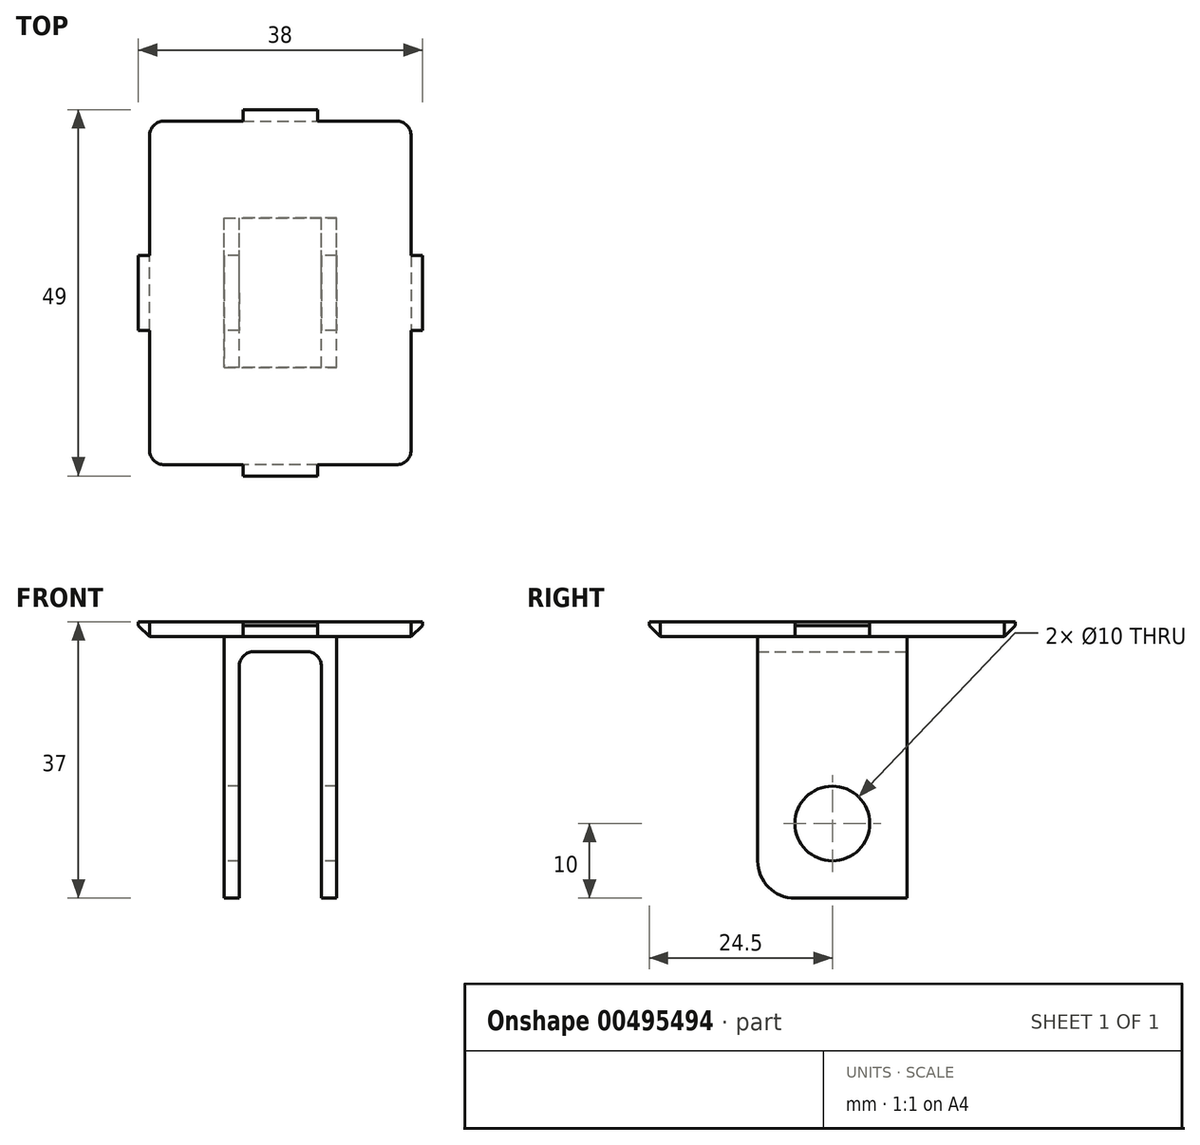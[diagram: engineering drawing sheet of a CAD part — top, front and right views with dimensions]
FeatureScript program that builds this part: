
annotation { "Feature Type Name" : "Feature", "Feature Type Description" : "" }
export const myFeature = defineFeature(function(context is Context, id is Id, definition is map)
    precondition{}
    {
        {
            var Q0;
            Q0=qCreatedBy(makeId("Front.planeOp"),FACE);
            var sketch = newSketch(context, id + "F0", { "sketchPlane" : qUnion([Q0])});
            skLineSegment(sketch, "E0", {"start": v(0, 71.67) * mm, "end": v(0, 0) * mm, "construction": true});
            skLineSegment(sketch, "E1", {"start": v(0, 0) * mm, "end": v(-98, 0) * mm, "construction": true});
            skLineSegment(sketch, "E2", {"start": v(0, 35) * mm, "end": v(-7.5, 35) * mm});
            skLineSegment(sketch, "E3", {"start": v(-7.5, 35) * mm, "end": v(-7.5, 0) * mm});
            skLineSegment(sketch, "E4", {"start": v(0, 33) * mm, "end": v(-3.5, 33) * mm});
            skLineSegment(sketch, "E5", {"start": v(-5.5, 31) * mm, "end": v(-5.5, 0) * mm});
            skLineSegment(sketch, "E6", {"start": v(-7.5, 0) * mm, "end": v(-5.5, 0) * mm});
            skPoint(sketch, "E7.visualSharp", {"position": v(-5.5, 33) * mm});
            skArc(sketch, "E7.filletArc", {"start": v(-3.5, 33) * mm, "mid": v(-4.91, 32.41) * mm, "end": v(-5.5, 31) * mm});
            skLineSegment(sketch, "E8.MirrorCS", {"start": v(0, 33) * mm, "end": v(3.5, 33) * mm});
            skLineSegment(sketch, "E9.MirrorCS", {"start": v(7.5, 0) * mm, "end": v(5.5, 0) * mm});
            skArc(sketch, "E10.MirrorCS", {"start": v(3.5, 33) * mm, "mid": v(4.91, 32.41) * mm, "end": v(5.5, 31) * mm});
            skLineSegment(sketch, "E11.MirrorCS", {"start": v(5.5, 31) * mm, "end": v(5.5, 0) * mm});
            skPoint(sketch, "E12.MirrorP", {"position": v(5.5, 33) * mm});
            skLineSegment(sketch, "E13.MirrorCS", {"start": v(0, 35) * mm, "end": v(7.5, 35) * mm});
            skLineSegment(sketch, "E14.MirrorCS", {"start": v(7.5, 35) * mm, "end": v(7.5, 0) * mm});
            skSolve(sketch);
        }
        {
            var Q0;
            Q0 = qSketchRegion(id + "F0", true);
            extrude(context, id + "F1", {"entities" : qUnion([Q0]), "depth" : 20 * mm});
        }
        {
            var Q0;
            Q0=makeQuery(id+"F1.opExtrude","SWEPT_FACE",FACE,{"disambiguationData":[OSD([sQuery(id+"F0.wireOp",EDGE,"E3")])]});
            var sketch = newSketch(context, id + "F2", { "sketchPlane" : qUnion([Q0])});
            skLineSegment(sketch, "E15.bottom", {"start": v(0, 20) * mm, "end": v(20, 20) * mm});
            skLineSegment(sketch, "E15.top", {"start": v(5, 0) * mm, "end": v(15, 0) * mm});
            skLineSegment(sketch, "E15.left", {"start": v(0, 20) * mm, "end": v(0, 5) * mm});
            skLineSegment(sketch, "E15.right", {"start": v(20, 20) * mm, "end": v(20, 5) * mm});
            skPoint(sketch, "E16", {"position": v(10, 10) * mm});
            skPoint(sketch, "E17.visualSharp", {"position": v(20, 0) * mm});
            skArc(sketch, "E17.filletArc", {"start": v(15, 0) * mm, "mid": v(18.54, 1.46) * mm, "end": v(20, 5) * mm});
            skPoint(sketch, "E18.visualSharp", {"position": v(0, 0) * mm});
            skArc(sketch, "E18.filletArc", {"start": v(0, 5) * mm, "mid": v(1.46, 1.46) * mm, "end": v(5, 0) * mm});
            skLineSegment(sketch, "E19", {"start": v(20, 5) * mm, "end": v(20, 0) * mm});
            skLineSegment(sketch, "E20", {"start": v(15, 0) * mm, "end": v(0, 0) * mm});
            skLineSegment(sketch, "E21.bottom", {"start": v(20, 20) * mm, "end": v(0, 20) * mm});
            skLineSegment(sketch, "E22.bottom", {"start": v(22.12, 19.96) * mm, "end": v(-3.3, 19.96) * mm});
            skLineSegment(sketch, "E22.top", {"start": v(22.12, -2.64) * mm, "end": v(-3.3, -2.64) * mm});
            skLineSegment(sketch, "E22.left", {"start": v(22.12, 19.96) * mm, "end": v(22.12, -2.64) * mm});
            skLineSegment(sketch, "E22.right", {"start": v(-3.3, 19.96) * mm, "end": v(-3.3, -2.64) * mm});
            skSolve(sketch);
        }
        {
            var Q0;
            Q0=sQuery(id+"F2.wireOp",VERTEX,"E16");
            var Q1;
            Q1=makeQuery(id+"F1.opExtrude","SWEPT_BODY",BODY,{"disambiguationData":[OSD([sQuery(id+"F0.wireOp",EDGE,"E2"),sQuery(id+"F0.wireOp",EDGE,"E3"),sQuery(id+"F0.wireOp",EDGE,"E4"),sQuery(id+"F0.wireOp",EDGE,"E5"),sQuery(id+"F0.wireOp",EDGE,"E6"),sQuery(id+"F0.wireOp",EDGE,"E7.filletArc"),sQuery(id+"F0.wireOp",EDGE,"E8.MirrorCS"),sQuery(id+"F0.wireOp",EDGE,"E9.MirrorCS"),sQuery(id+"F0.wireOp",EDGE,"E10.MirrorCS"),sQuery(id+"F0.wireOp",EDGE,"E11.MirrorCS"),sQuery(id+"F0.wireOp",EDGE,"E13.MirrorCS"),sQuery(id+"F0.wireOp",EDGE,"E14.MirrorCS")])]});
            hole(context, id + "F3", {"style" : HoleStyle.SIMPLE, "endStyle" : HoleEndStyle.BLIND, "holeDiameter" : 10 * mm, "holeDepth" : 45 * mm, "isTappedThrough" : true, "tappedDepth" : 12 * mm, "tapClearance" : 3, "startFromSketch" : true, "locations" : qUnion([Q0]), "scope" : qUnion([Q1])});
        }
        {
            var Q0;
            Q0=makeQuery(id+"F1.opExtrude","SWEPT_FACE",FACE,{"disambiguationData":[OSD([sQuery(id+"F0.wireOp",EDGE,"E2"),sQuery(id+"F0.wireOp",EDGE,"E13.MirrorCS")])]});
            var sketch = newSketch(context, id + "F4", { "sketchPlane" : qUnion([Q0])});
            skLineSegment(sketch, "E23.bottom", {"start": v(15.5, -33) * mm, "end": v(-15.5, -33) * mm});
            skLineSegment(sketch, "E23.top", {"start": v(15.5, 13) * mm, "end": v(0, 13) * mm});
            skLineSegment(sketch, "E23.left", {"start": v(17.5, -31) * mm, "end": v(17.5, 11) * mm});
            skLineSegment(sketch, "E23.right", {"start": v(-17.5, -31) * mm, "end": v(-17.5, 11) * mm});
            skPoint(sketch, "E24.visualSharp", {"position": v(17.5, -33) * mm});
            skArc(sketch, "E24.filletArc", {"start": v(15.5, -33) * mm, "mid": v(16.91, -32.41) * mm, "end": v(17.5, -31) * mm});
            skPoint(sketch, "E25.visualSharp", {"position": v(-17.5, -33) * mm});
            skArc(sketch, "E25.filletArc", {"start": v(-17.5, -31) * mm, "mid": v(-16.91, -32.41) * mm, "end": v(-15.5, -33) * mm});
            skPoint(sketch, "E26.visualSharp", {"position": v(-17.5, 13) * mm});
            skArc(sketch, "E26.filletArc", {"start": v(-15.5, 13) * mm, "mid": v(-16.91, 12.41) * mm, "end": v(-17.5, 11) * mm});
            skPoint(sketch, "E27.visualSharp", {"position": v(17.5, 13) * mm});
            skArc(sketch, "E27.filletArc", {"start": v(17.5, 11) * mm, "mid": v(16.91, 12.41) * mm, "end": v(15.5, 13) * mm});
            skLineSegment(sketch, "E28", {"start": v(-17.5, -10) * mm, "end": v(17.5, -10) * mm, "construction": true});
            skLineSegment(sketch, "E29", {"start": v(0, 13) * mm, "end": v(0, -33) * mm, "construction": true});
            skLineSegment(sketch, "E30.bottom", {"start": v(0, 13) * mm, "end": v(-5, 13) * mm});
            skLineSegment(sketch, "E30.top", {"start": v(0, 14.5) * mm, "end": v(-5, 14.5) * mm});
            skLineSegment(sketch, "E30.right", {"start": v(-5, 13) * mm, "end": v(-5, 14.5) * mm});
            skLineSegment(sketch, "E31.MirrorCS", {"start": v(0, 16) * mm, "end": v(0, 14.5) * mm});
            skLineSegment(sketch, "E32.MirrorCS", {"start": v(0, 14.5) * mm, "end": v(5, 14.5) * mm});
            skLineSegment(sketch, "E33.MirrorCS", {"start": v(5, 13) * mm, "end": v(5, 14.5) * mm});
            skLineSegment(sketch, "E34.trimOffspring", {"start": v(-5, 13) * mm, "end": v(-15.5, 13) * mm});
            skLineSegment(sketch, "E35.MirrorCS", {"start": v(-5, -33) * mm, "end": v(-5, -34.5) * mm});
            skLineSegment(sketch, "E36.MirrorCS", {"start": v(0, -34.5) * mm, "end": v(5, -34.5) * mm});
            skLineSegment(sketch, "E37.MirrorCS", {"start": v(5, -33) * mm, "end": v(5, -34.5) * mm});
            skLineSegment(sketch, "E38.MirrorCS", {"start": v(0, -34.5) * mm, "end": v(-5, -34.5) * mm});
            skLineSegment(sketch, "E39.top", {"start": v(-17.5, -15) * mm, "end": v(-19, -15) * mm});
            skLineSegment(sketch, "E39.left", {"start": v(-17.5, -10) * mm, "end": v(-17.5, -15) * mm});
            skLineSegment(sketch, "E39.right", {"start": v(-19, -10) * mm, "end": v(-19, -15) * mm});
            skLineSegment(sketch, "E40.MirrorCS", {"start": v(-19, -10) * mm, "end": v(-19, -5) * mm});
            skLineSegment(sketch, "E41.MirrorCS", {"start": v(-17.5, -5) * mm, "end": v(-19, -5) * mm});
            skLineSegment(sketch, "E42.MirrorCS", {"start": v(19, -10) * mm, "end": v(19, -15) * mm});
            skLineSegment(sketch, "E43.MirrorCS", {"start": v(19, -10) * mm, "end": v(19, -5) * mm});
            skLineSegment(sketch, "E44.MirrorCS", {"start": v(17.5, -5) * mm, "end": v(19, -5) * mm});
            skLineSegment(sketch, "E45.MirrorCS", {"start": v(17.5, -15) * mm, "end": v(19, -15) * mm});
            skSolve(sketch);
        }
        {
            var Q0;
            Q0=makeQuery(id+"F4.imprint","IMPRINT",FACE,{"disambiguationData":[TD([[makeQuery(id+"F4.imprint","IMPRINT",EDGE,{"derivedFrom":sQuery(id+"F4.wireOp",EDGE,"E23.bottom")}),-1.0]])]});
            var Q1;
            {var subQ0=sQuery(id+"F0.wireOp",EDGE,"E2");Q1=makeQuery(id+"F4.imprint","IMPRINT",FACE,{"disambiguationData":[TD([[makeQuery(id+"F4.imprint","IMPRINT",EDGE,{"derivedFrom":makeQuery(id+"F1.opExtrude","SWEPT_EDGE",EDGE,{"disambiguationData":[OSD([subQ0,sQuery(id+"F0.wireOp",EDGE,"E3")])]})}),-1.0]])]});}
            var Q2;
            Q2=makeQuery(id+"F4.imprint","IMPRINT",FACE,{"disambiguationData":[TD([[makeQuery(id+"F4.imprint","IMPRINT",EDGE,{"derivedFrom":sQuery(id+"F4.wireOp",EDGE,"E39.top")}),-1.0]])]});
            var Q3;
            {var subQ0=sQuery(id+"F4.wireOp",EDGE,"E30.bottom");Q3=makeQuery(id+"F4.imprint","IMPRINT",FACE,{"disambiguationData":[TD([[makeQuery(id+"F4.imprint","IMPRINT",EDGE,{"derivedFrom":subQ0}),-1.0]])]});}
            var Q4;
            Q4=makeQuery(id+"F4.imprint","IMPRINT",FACE,{"disambiguationData":[TD([[makeQuery(id+"F4.imprint","IMPRINT",EDGE,{"derivedFrom":sQuery(id+"F4.wireOp",EDGE,"E42.MirrorCS")}),-1.0]])]});
            var Q5;
            {var subQ1=sQuery(id+"F4.wireOp",EDGE,"E35.MirrorCS");Q5=makeQuery(id+"F4.imprint","IMPRINT",FACE,{"disambiguationData":[TD([[makeQuery(id+"F4.imprint","IMPRINT",EDGE,{"derivedFrom":subQ1}),1.0]])]});}
            extrude(context, id + "F5", {"entities" : qUnion([Q0, Q1, Q2, Q3, Q4, Q5]), "operationType" : NewBodyOperationType.ADD, "depth" : 2 * mm});
        }
        {
            var Q0;
            {var subQ0=sQuery(id+"F2.wireOp",EDGE,"E19");Q0=makeQuery(id+"F2.imprint","IMPRINT",FACE,{"disambiguationData":[TD([[makeQuery(id+"F2.imprint","IMPRINT",EDGE,{"derivedFrom":subQ0}),-1.0]])]});}
            var Q1;
            {var subQ3=sQuery(id+"F2.wireOp",EDGE,"E18.filletArc");Q1=makeQuery(id+"F2.imprint","IMPRINT",FACE,{"disambiguationData":[TD([[makeQuery(id+"F2.imprint","IMPRINT",EDGE,{"derivedFrom":subQ3}),-1.0]])]});}
            extrude(context, id + "F6", {"entities" : qUnion([Q0, Q1]), "operationType" : NewBodyOperationType.REMOVE, "endBound" : BoundingType.THROUGH_ALL, "oppositeDirection" : true, "depth" : 25 * mm});
        }
        {
            var Q0;
            Q0=makeQuery(id+"F5.opExtrude","CAP_EDGE",EDGE,{"disambiguationData":[OSD([sQuery(id+"F4.wireOp",EDGE,"E39.right"),sQuery(id+"F4.wireOp",EDGE,"E40.MirrorCS")])],"isStart":true});
            var Q1;
            Q1=makeQuery(id+"F5.opExtrude","CAP_EDGE",EDGE,{"disambiguationData":[OSD([sQuery(id+"F4.wireOp",EDGE,"E30.top"),sQuery(id+"F4.wireOp",EDGE,"E32.MirrorCS")])],"isStart":true});
            var Q2;
            Q2=makeQuery(id+"F5.opExtrude","CAP_EDGE",EDGE,{"disambiguationData":[OSD([sQuery(id+"F4.wireOp",EDGE,"E42.MirrorCS"),sQuery(id+"F4.wireOp",EDGE,"E43.MirrorCS")])],"isStart":true});
            var Q3;
            Q3=makeQuery(id+"F5.opExtrude","CAP_EDGE",EDGE,{"disambiguationData":[OSD([sQuery(id+"F4.wireOp",EDGE,"E36.MirrorCS"),sQuery(id+"F4.wireOp",EDGE,"E38.MirrorCS")])],"isStart":true});
            chamfer(context, id + "F7", {"entities" : qUnion([Q0, Q1, Q2, Q3]), "width" : 1.5 * mm, "tangentPropagation" : true});
        }
    });
